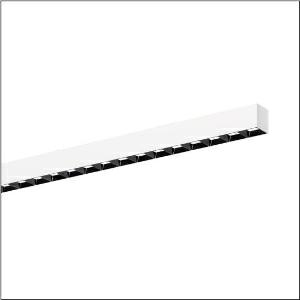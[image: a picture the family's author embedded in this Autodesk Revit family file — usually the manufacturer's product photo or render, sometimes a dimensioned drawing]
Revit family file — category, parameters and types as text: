
# Revit family: silica_r__21_51mx21tbt5w_e527
name_source: partatom
category: Lighting Fixtures
units: mm (PartAtom-declared; Revit-internal decimal feet)

## family parameters
Cut with Voids When Loaded = No
Host = Face
Light Source = No
Part Type = Normal
Room Calculation Point = No
Round Connector Dimension = Use Diameter
Shared = No

## types (1)
- --- (1 x LED, 4650 lm, 40.3 W, 6500K)
    Apparent Load = 40 VA
    CIE Flux Codes = 85 99 100 100 100
    Color Rendering = 80
    Color Temperature = 6500K
    Default Elevation = 1800 mm
    Description = Silica® 21, office luminaire, primary light control with darklight reflector, of PMMA, black, CAT 2 (L<= 3000cd/m²), light emission: direct distribution, primary light characteristic: symmetric, installation type: surface-mounted, LED, rated luminous flux: 4.650lm, luminous efficacy: 110lm/W, light colour: 8tw, colour temperature: 2700..6500K, control gear: ECG DALI, with terminal, 3+2-pole, max. 2.5mm², mains connection: 220..240V, AC, 50/60Hz, rated input power: 42.3W, luminaire housing, of aluminium, traffic white (RAL 9016), length: 1.504mm, width: 53mm, height: 53mm, protection rating (complete): IP20, insulation class (complete): insulation class I (protective earthing), certification: CE, permissible operating ambient temperature: 0..+35°C, standard: EN 50419, packaging unit: 1 piece
    Height = 0 mm  [stored 0 ft]
    Lamp = 1 x LED
    Lamp Light Flux = 4650 lm
    Lamp Power = 40.3 W
    Lamp count = 1
    Length = 1504 mm
    Luminous efficacy = 115 lm/W
    Manufacturer = Siteco
    ModVariant = No
    Model = 51MX21TBT5W
    Mounting Place = Ceiling
    Mounting Type = Recessed
    Number of Poles = 1
    OnlyDefault = Yes
    Power Factor = 1
    Product Name = Silica® 21
    Product group = office luminaire | ceiling recessed
    ProductGroupID = 401
    Protection Class = Protection class I
    Protection Degree = IP 20
    RLX_Detail_Level = 1
    RLX_Emergency_Light_Flux = 0 lm
    RLX_Emergency_Type = 0
    RLX_Emergency_Type_DB = No
    RlxData = <blob elided: 41477 chars, md5=62dfe54b>
    Socket = socket
    Standby Power = 0 W
    System Light Flux = 4650 lm
    System Power = 40 W
    Type Comments = individual setting
    Type Image = l_1297779.jpg
    URL = http://relux.com
    VarID = @adj_071407
    Voltage = 0 V
    Weight = 0.00 kg
    Width = 53 mm

note: [stored X ft] marks values corroborated as IEEE doubles in the binary element streams (Revit-internal decimal feet)

## geometry (parser evidence)
native form markers: Blend x4, Sweep x11
no freeform markers — native parametric forms only
